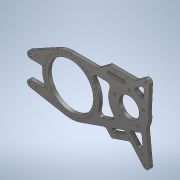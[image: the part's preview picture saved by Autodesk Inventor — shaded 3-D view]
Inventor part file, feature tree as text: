
AUTODESK INVENTOR PART (.ipt)
format: ipt  version: 2021 (Build 250183000, 183)  size: 573,440 bytes
history: native  units: in
note: dims shown in document units (in); Inventor stores cm internally (conversion verified against a paired STEP export)
features: sketch x21, extrude x16, hole x5, fillet x4, chamfer x1, projected_geometry x1
ambient origin geometry x8: Origin, YZ Plane, XZ Plane, XY Plane, X Axis, Y Axis, Z Axis, Center Point
bodies: Body1 (feature_tree)
feature tree (48):
  extrude  "Extrusion13"  Depth=0.5in TaperAngle=0.0deg
  hole  "Hole4"  [1 undecoded]
  extrude  "Extrusion15"  Depth=1.0in
  extrude  "Extrusion16"  Depth=0.5in TaperAngle=0.0deg
  hole  "Hole6"  [1 undecoded]
  extrude  "Extrusion17"  Depth=1.0in
  hole  "Hole7"  [1 undecoded]
  hole  "Hole9"  [1 undecoded]
  hole  "Hole10"  [1 undecoded]
  extrude  "Extrusion18"  Depth=1.0in
  extrude  "Extrusion19"  Depth=0.239in
  sketch  "Sketch33"  dims[d183=0.257in d184=0.75in d185=0.438in d186=0.25in d187=0.5635in d188=1.0in d189=0.8108in d191=1.0in]
  extrude  "Extrusion21"  Depth=0.5in
  extrude  "Extrusion22"  Depth=1.0in
  extrude  "Extrusion23"  Depth=0.75in
  extrude  "Extrusion24"  Depth=0.75in
  fillet  "Fillet2"  Radius=0.25in
  extrude  "Extrusion25"  Depth=1.0in TaperAngle=0.0deg
  extrude  "Extrusion26"  Depth=1.0in TaperAngle=0.0deg
  fillet  "Fillet3"  Radius=0.75in
  extrude  "Extrusion27"  Depth=0.75in
  chamfer  "Chamfer1"  Distance=0.25in
  sketch  "Sketch40"  dims[d211=0.75in d212=0.75in d213=0.25in]
  extrude  "Extrusion29"  Depth=1.0in TaperAngle=0.0deg
  extrude  "Extrusion30"  Depth=0.25in
  fillet  "Fillet4"  Radius=1.0in
  fillet  "Fillet5"  Radius=0.75in
  extrude  "Extrusion32"  Depth=1.0in TaperAngle=0.0deg
  sketch  "Sketch14"  dims[d96=8.5in d97=2.16in d98=9.0in d99=5.5in d100=1.0in d101=1.0in d102=6.0in d103=6.0in d104=3.718in d105=1.0in d108=10.718in d109=1.5in d111=0.5in d112=0.0in]
  sketch  "Sketch15"  dims[d113=0.386in d114=0.75in d115=0.762in d116=0.25in d117=0.5635in d118=0.484in d119=0.8108in d132=5.0in]
  sketch  "Sketch18"  dims[d133=17.223in d134=1.0in]
  sketch  "Sketch19"  dims[d135=1.0in d136=0.5in d137=0.0in]
  sketch  "Sketch20"  dims[d138=1.0in d140=4.0in]
  sketch  "Sketch21"  dims[d141=0.5in d142=0.0in d143=1.0in]
  sketch  "Sketch23"  dims[d144=1.625in]
  sketch  "Sketch27"  dims[d145=0.177in d146=0.75in d147=0.332in d148=0.25in d149=0.5635in d150=0.484in d151=0.8108in d155=1.0in d156=0.0in]
  sketch  "Sketch29"  dims[d157=1.625in]
  sketch  "Sketch31"  dims[d159=0.177in d160=0.75in d161=0.332in d162=0.25in d163=0.5635in d164=1.0in d165=0.8108in d178=7.75in]
  sketch  "Sketch32"  dims[d179=3.5433in d181=360.0deg]
  sketch  "Sketch34"  dims[d192=0.0481in d193=1.0in]
  sketch  "Sketch35"  dims[d194=0.3526in d197=0.239in]
  sketch  "Sketch36"  dims[d198=0.1195in d199=0.5in]
  sketch  "Sketch38"  dims[d200=0.266in d201=0.75in d202=0.507in d203=0.25in d204=0.5635in d205=1.0in d206=0.8108in d207=0.1718in]
  sketch  "Sketch39"  dims[d208=15.0deg d210=0.75in]
  sketch  "Sketch42"  dims[d214=0.5in d215=1.0in d216=0.0in]
  sketch  "Sketch43"  dims[d217=0.25in d218=1.0in d219=0.0in d220=0.75in]
  sketch  "Sketch45"  dims[d221=0.5in d223=0.75in d231=0.25in d232=1.0in d233=0.0in d234=0.25in d235=1.0in d236=0.0in d237=0.75in d238=1.0in d239=0.0in d242=1.0in d243=0.0in d244=0.25in d247=0.75in d249=0.75in d250=0.5in d251=2.8in d252=0.375in d253=1.25in d255=0.75in d256=0.75in d257=1.0in d258=0.0in d259=0.25in d260=1.0in d261=0.0in d262=0.25in d263=0.5in d264=1.0in d265=0.0in d266=0.0156in d267=0.125in d268=45.0deg d284=1.0in d285=0.0in d296=6.75in d297=1.0in d298=0.0in d303=3.005in d304=8.715in d305=6.5in d306=0.5in d307=0.5in d308=4.44in d309=0.325in d310=1.9685in d312=360.0deg d314=1.0in d315=0.0in d316=0.061in d283=0.5in d286=0.0344in]
  projected_geometry  "Project Cut Edges1"
note: 5 required parameter values undecoded (feature->parameter linkage not recoverable at this tier; creation-order binding heuristic only, values carry confidence <= 0.55)
